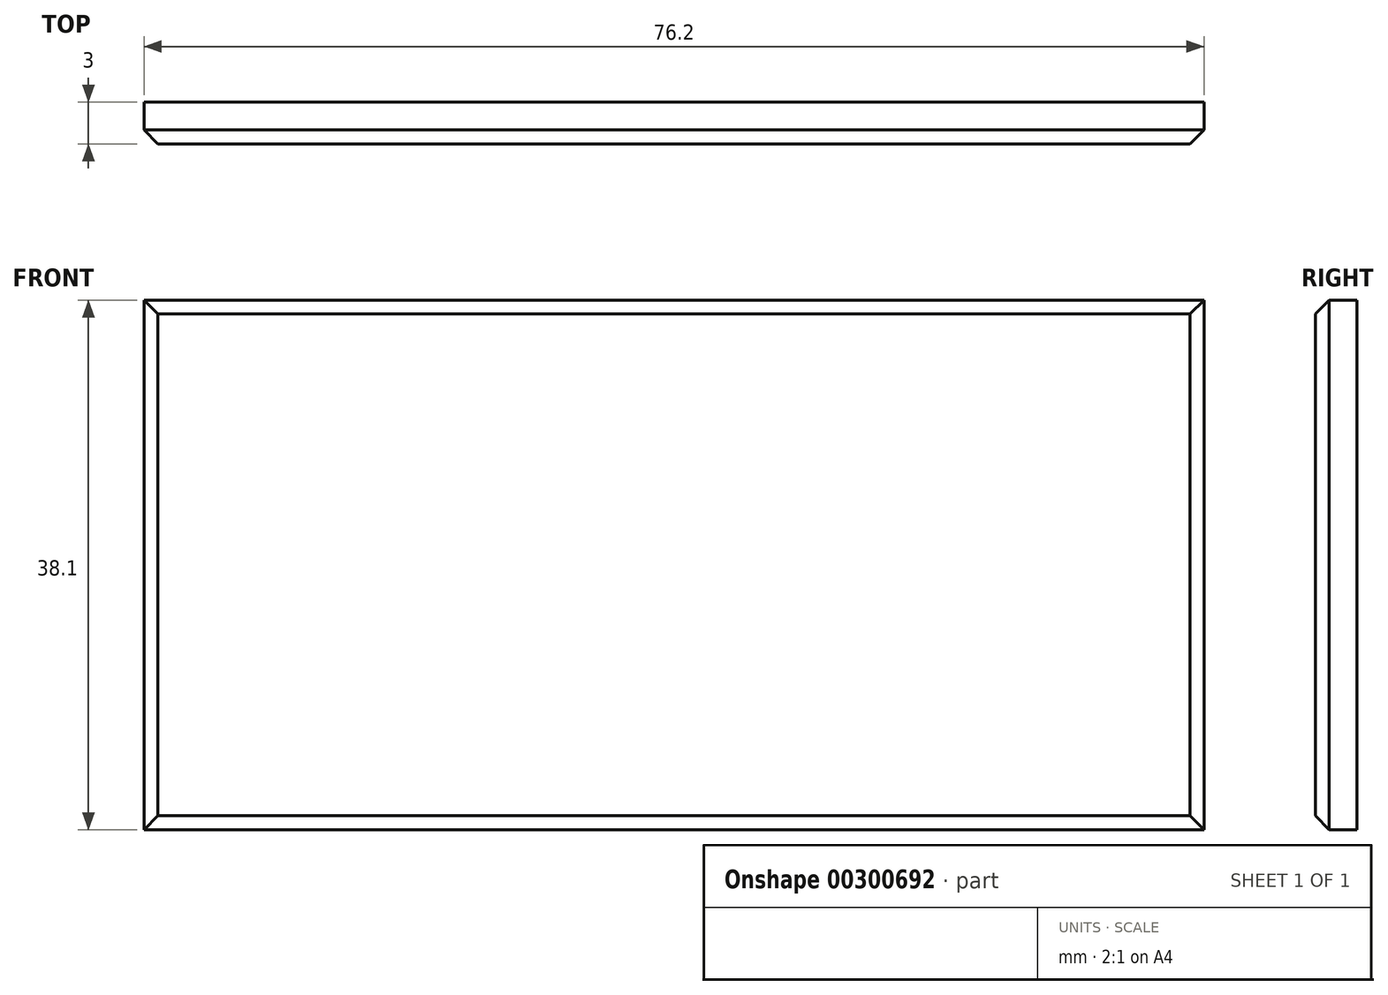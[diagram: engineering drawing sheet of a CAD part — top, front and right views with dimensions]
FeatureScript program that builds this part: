
annotation { "Feature Type Name" : "Feature", "Feature Type Description" : "" }
export const myFeature = defineFeature(function(context is Context, id is Id, definition is map)
    precondition{}
    {
        {
            var Q0;
            Q0=qCreatedBy(makeId("Front.planeOp"),FACE);
            var sketch = newSketch(context, id + "F0", { "sketchPlane" : qUnion([Q0])});
            skLineSegment(sketch, "E0.bottom", {"start": v(38.1, 19.05) * mm, "end": v(-38.1, 19.05) * mm});
            skLineSegment(sketch, "E0.top", {"start": v(38.1, -19.05) * mm, "end": v(-38.1, -19.05) * mm});
            skLineSegment(sketch, "E0.left", {"start": v(38.1, 19.05) * mm, "end": v(38.1, -19.05) * mm});
            skLineSegment(sketch, "E0.right", {"start": v(-38.1, 19.05) * mm, "end": v(-38.1, -19.05) * mm});
            skPoint(sketch, "E0.middle", {"position": v(0, 0) * mm});
            skSolve(sketch);
        }
        {
            var Q0;
            Q0 = qSketchRegion(id + "F0", true);
            extrude(context, id + "F1", {"entities" : qUnion([Q0]), "depth" : 3 * mm});
        }
        {
            var Q0;
            Q0=makeQuery(id+"F1.opExtrude","CAP_EDGE",EDGE,{"disambiguationData":[OSD([sQuery(id+"F0.wireOp",EDGE,"E0.top")])],"isStart":false});
            var Q1;
            Q1=makeQuery(id+"F1.opExtrude","CAP_EDGE",EDGE,{"disambiguationData":[OSD([sQuery(id+"F0.wireOp",EDGE,"E0.right")])],"isStart":false});
            var Q2;
            Q2=makeQuery(id+"F1.opExtrude","CAP_EDGE",EDGE,{"disambiguationData":[OSD([sQuery(id+"F0.wireOp",EDGE,"E0.bottom")])],"isStart":false});
            var Q3;
            Q3=makeQuery(id+"F1.opExtrude","CAP_EDGE",EDGE,{"disambiguationData":[OSD([sQuery(id+"F0.wireOp",EDGE,"E0.left")])],"isStart":false});
            chamfer(context, id + "F2", {"entities" : qUnion([Q0, Q1, Q2, Q3]), "width" : 1 * mm, "tangentPropagation" : true});
        }
    });
